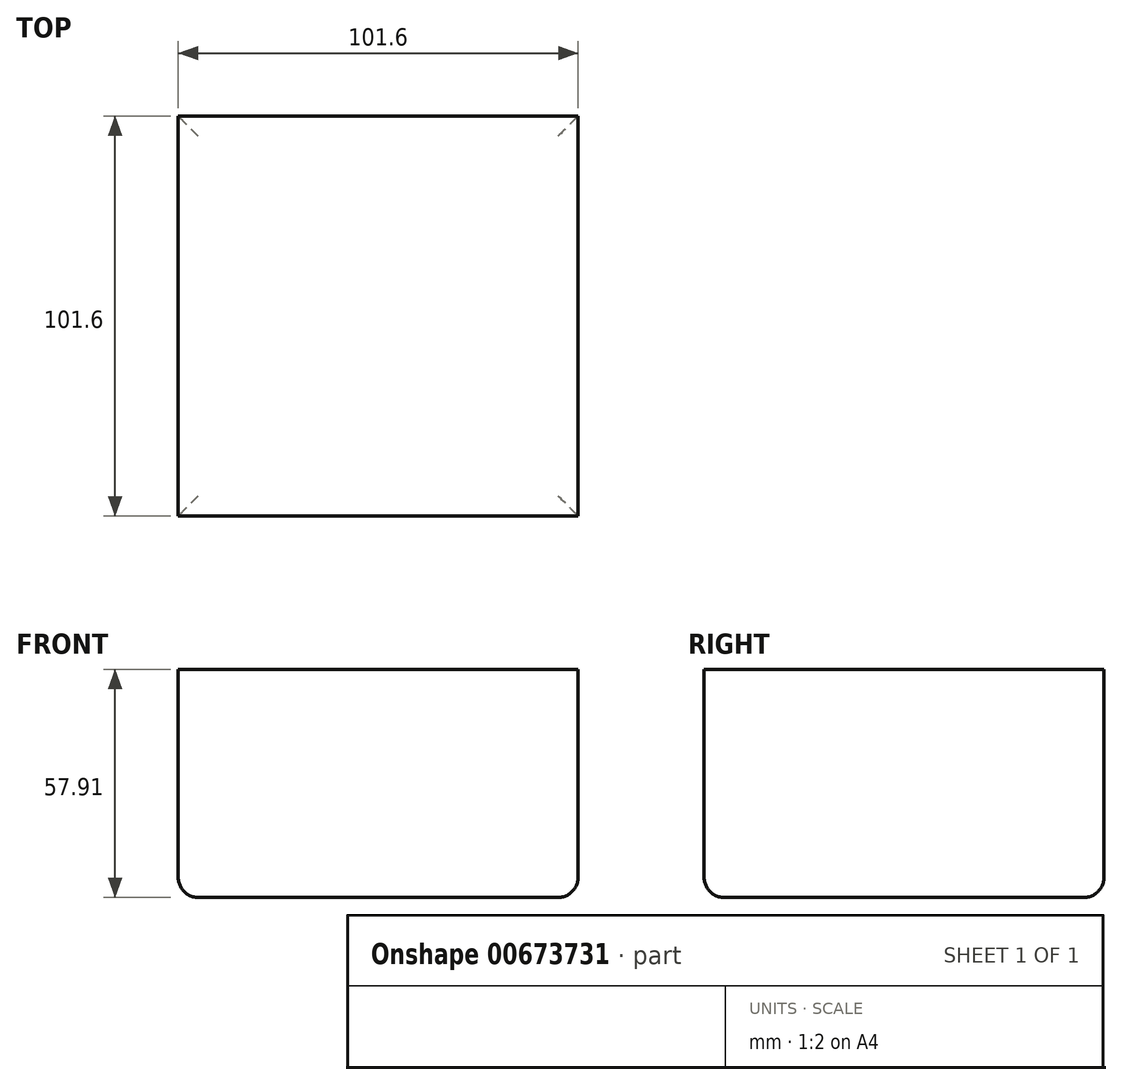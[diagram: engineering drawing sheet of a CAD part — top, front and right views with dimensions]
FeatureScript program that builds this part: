
annotation { "Feature Type Name" : "Feature", "Feature Type Description" : "" }
export const myFeature = defineFeature(function(context is Context, id is Id, definition is map)
    precondition{}
    {
        {
            var Q0;
            Q0=qCreatedBy(makeId("Top.planeOp"),FACE);
            var sketch = newSketch(context, id + "F0", { "sketchPlane" : qUnion([Q0])});
            skLineSegment(sketch, "E0.bottom", {"start": v(50.8, 50.8) * mm, "end": v(-50.8, 50.8) * mm});
            skLineSegment(sketch, "E0.top", {"start": v(50.8, -50.8) * mm, "end": v(-50.8, -50.8) * mm});
            skLineSegment(sketch, "E0.left", {"start": v(50.8, 50.8) * mm, "end": v(50.8, -50.8) * mm});
            skLineSegment(sketch, "E0.right", {"start": v(-50.8, 50.8) * mm, "end": v(-50.8, -50.8) * mm});
            skPoint(sketch, "E0.middle", {"position": v(0, 0) * mm});
            skSolve(sketch);
        }
        {
            var Q0;
            Q0=makeQuery(id+"F0.imprint","IMPRINT",FACE,{"disambiguationData":[TD([[makeQuery(id+"F0.imprint","IMPRINT",EDGE,{"derivedFrom":sQuery(id+"F0.wireOp",EDGE,"E0.bottom")}),1.0]])]});
            extrude(context, id + "F1", {"entities" : qUnion([Q0]), "depth" : 57.9 * mm, "offsetDistance" : 25.4 * mm});
        }
        {
            var Q0;
            Q0=makeQuery(id+"F1.opExtrude","CAP_FACE",FACE,{"disambiguationData":[OSD([sQuery(id+"F0.wireOp",EDGE,"E0.bottom"),sQuery(id+"F0.wireOp",EDGE,"E0.top"),sQuery(id+"F0.wireOp",EDGE,"E0.left"),sQuery(id+"F0.wireOp",EDGE,"E0.right")])],"isStart":true});
            fillet(context, id + "F2", {"entities" : qUnion([Q0]), "tangentPropagation" : true, "radius" : 5.08 * mm, "defaultsChanged" : false, "vertexSettings" : [], "allowEdgeOverflow" : false});
        }
    });
